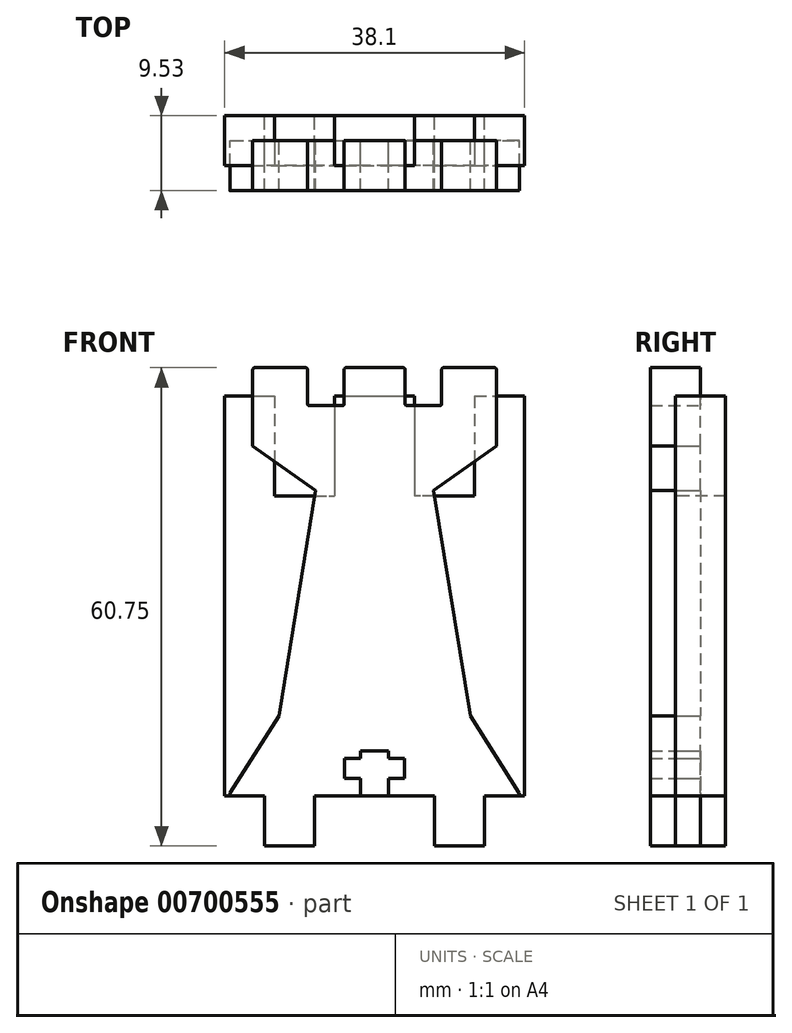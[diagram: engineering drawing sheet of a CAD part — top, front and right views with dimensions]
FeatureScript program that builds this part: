
annotation { "Feature Type Name" : "Feature", "Feature Type Description" : "" }
export const myFeature = defineFeature(function(context is Context, id is Id, definition is map)
    precondition{}
    {
        {
            var Q0;
            Q0=qCreatedBy(makeId("Front.planeOp"),FACE);
            var sketch = newSketch(context, id + "F0", { "sketchPlane" : qUnion([Q0])});
            skLineSegment(sketch, "E0.bottom", {"start": v(-6.35, 0) * mm, "end": v(7.62, 0) * mm});
            skLineSegment(sketch, "E1.bottom", {"start": v(-19.05, 0) * mm, "end": v(-13.97, 0) * mm});
            skLineSegment(sketch, "E1.top", {"start": v(-19.05, 50.8) * mm, "end": v(19.05, 50.8) * mm});
            skLineSegment(sketch, "E1.left", {"start": v(-19.05, 0) * mm, "end": v(-19.05, 50.8) * mm});
            skLineSegment(sketch, "E1.right", {"start": v(19.05, 0) * mm, "end": v(19.05, 50.8) * mm});
            skLineSegment(sketch, "E2.top", {"start": v(7.62, -6.35) * mm, "end": v(13.97, -6.35) * mm});
            skLineSegment(sketch, "E2.left", {"start": v(7.62, 0) * mm, "end": v(7.62, -6.35) * mm});
            skLineSegment(sketch, "E2.right", {"start": v(13.97, 0) * mm, "end": v(13.97, -6.35) * mm});
            skLineSegment(sketch, "E3.MirrorCS", {"start": v(6.35, 0) * mm, "end": v(-7.62, 0) * mm});
            skLineSegment(sketch, "E4.MirrorCS", {"start": v(19.05, 0) * mm, "end": v(13.97, 0) * mm});
            skLineSegment(sketch, "E5.MirrorCS", {"start": v(-7.62, -6.35) * mm, "end": v(-13.97, -6.35) * mm});
            skLineSegment(sketch, "E6.MirrorCS", {"start": v(-7.62, 0) * mm, "end": v(-7.62, -6.35) * mm});
            skLineSegment(sketch, "E7.MirrorCS", {"start": v(-13.97, 0) * mm, "end": v(-13.97, -6.35) * mm});
            skLineSegment(sketch, "E8.trimOffspring", {"start": v(-13.97, 0) * mm, "end": v(-19.05, 0) * mm});
            skLineSegment(sketch, "E9.trimOffspring", {"start": v(7.62, 0) * mm, "end": v(-6.35, 0) * mm});
            skLineSegment(sketch, "E10.trimOffspring", {"start": v(13.97, 0) * mm, "end": v(19.05, 0) * mm});
            skLineSegment(sketch, "E11.trimOffspring", {"start": v(-7.62, 0) * mm, "end": v(6.35, 0) * mm});
            skSolve(sketch);
        }
        {
            var Q0;
            Q0 = qSketchRegion(id + "F0", true);
            extrude(context, id + "F1", {"entities" : qUnion([Q0]), "depth" : 3.17 * mm, "offsetDistance" : 25.4 * mm, "hasSecondDirection" : true, "secondDirectionOppositeDirection" : true, "secondDirectionDepth" : 3.17 * mm});
        }
        {
            var Q0;
            Q0=makeQuery(id+"F1.opExtrude","CAP_FACE",FACE,{"disambiguationData":[OSD([sQuery(id+"F0.wireOp",EDGE,"E0.top"),sQuery(id+"F0.wireOp",EDGE,"E0.left"),sQuery(id+"F0.wireOp",EDGE,"E0.right"),sQuery(id+"F0.wireOp",EDGE,"E1.bottom"),sQuery(id+"F0.wireOp",EDGE,"E1.top"),sQuery(id+"F0.wireOp",EDGE,"E1.left"),sQuery(id+"F0.wireOp",EDGE,"E1.right")])],"isStart":false});
            var sketch = newSketch(context, id + "F2", { "sketchPlane" : qUnion([Q0])});
            skPoint(sketch, "E12.endSnap0", {"position": v(5.08, 50.8) * mm});
            skLineSegment(sketch, "E13", {"start": v(5.08, 50.8) * mm, "end": v(5.08, 38.1) * mm, "construction": true});
            skLineSegment(sketch, "E14", {"start": v(-5.08, 50.8) * mm, "end": v(-5.08, 38.1) * mm, "construction": true});
            skLineSegment(sketch, "E15", {"start": v(-12.7, 50.8) * mm, "end": v(-12.7, 38.1) * mm});
            skLineSegment(sketch, "E16", {"start": v(-12.7, 38.1) * mm, "end": v(-5.08, 38.1) * mm});
            skLineSegment(sketch, "E17", {"start": v(-5.08, 50.8) * mm, "end": v(-5.08, 38.1) * mm});
            skLineSegment(sketch, "E18", {"start": v(5.08, 50.8) * mm, "end": v(5.08, 38.1) * mm});
            skLineSegment(sketch, "E19", {"start": v(12.7, 50.8) * mm, "end": v(12.7, 38.1) * mm});
            skLineSegment(sketch, "E20", {"start": v(12.7, 38.1) * mm, "end": v(5.08, 38.1) * mm});
            skLineSegment(sketch, "E21", {"start": v(-12.7, 50.8) * mm, "end": v(-5.08, 50.8) * mm});
            skLineSegment(sketch, "E22", {"start": v(12.7, 50.8) * mm, "end": v(5.08, 50.8) * mm});
            skSolve(sketch);
        }
        {
            var Q0;
            Q0 = qSketchRegion(id + "F2", true);
            extrude(context, id + "F3", {"entities" : qUnion([Q0]), "operationType" : NewBodyOperationType.REMOVE, "oppositeDirection" : true, "depth" : 25.4 * mm, "offsetDistance" : 25.4 * mm});
        }
        {
            var Q0;
            Q0=qCreatedBy(makeId("Front.planeOp"),FACE);
            var sketch = newSketch(context, id + "F4", { "sketchPlane" : qUnion([Q0])});
            skLineSegment(sketch, "E23", {"start": v(-18.12, 0) * mm, "end": v(-13.97, 0) * mm});
            skLineSegment(sketch, "E24", {"start": v(-13.97, 0) * mm, "end": v(-13.97, -6.35) * mm});
            skLineSegment(sketch, "E25", {"start": v(-13.97, -6.35) * mm, "end": v(-7.62, -6.35) * mm});
            skLineSegment(sketch, "E26", {"start": v(-7.62, -6.35) * mm, "end": v(-7.62, 0) * mm});
            skLineSegment(sketch, "E27", {"start": v(-7.62, 0) * mm, "end": v(7.62, 0) * mm});
            skLineSegment(sketch, "E28", {"start": v(7.62, 0) * mm, "end": v(7.62, -6.35) * mm});
            skLineSegment(sketch, "E29", {"start": v(7.62, -6.35) * mm, "end": v(13.97, -6.35) * mm});
            skLineSegment(sketch, "E30", {"start": v(13.97, -6.35) * mm, "end": v(13.97, 0) * mm});
            skLineSegment(sketch, "E31", {"start": v(13.97, 0) * mm, "end": v(18.12, 0) * mm});
            skLineSegment(sketch, "E32", {"start": v(18.33, 0.39) * mm, "end": v(12.15, 10.17) * mm});
            skLineSegment(sketch, "E33", {"start": v(7.5, 38.81) * mm, "end": v(15.48, 44.47) * mm});
            skLineSegment(sketch, "E34", {"start": v(15.48, 44.47) * mm, "end": v(15.48, 54.15) * mm});
            skLineSegment(sketch, "E35", {"start": v(15.22, 54.4) * mm, "end": v(8.78, 54.4) * mm});
            skLineSegment(sketch, "E36", {"start": v(8.52, 54.15) * mm, "end": v(8.52, 49.82) * mm});
            skLineSegment(sketch, "E37", {"start": v(8.27, 49.57) * mm, "end": v(4.12, 49.57) * mm});
            skLineSegment(sketch, "E38", {"start": v(3.86, 49.82) * mm, "end": v(3.86, 54.15) * mm});
            skLineSegment(sketch, "E39", {"start": v(3.61, 54.4) * mm, "end": v(0, 54.4) * mm});
            skLineSegment(sketch, "E40.MirrorCS", {"start": v(13.97, 0) * mm, "end": v(13.97, -6.35) * mm});
            skLineSegment(sketch, "E41.MirrorCS", {"start": v(-3.86, 49.82) * mm, "end": v(-3.86, 54.15) * mm});
            skLineSegment(sketch, "E42.MirrorCS", {"start": v(-3.61, 54.4) * mm, "end": v(0, 54.4) * mm});
            skLineSegment(sketch, "E43.MirrorCS", {"start": v(13.97, -6.35) * mm, "end": v(7.62, -6.35) * mm});
            skLineSegment(sketch, "E44.MirrorCS", {"start": v(7.62, -6.35) * mm, "end": v(7.62, 0) * mm});
            skLineSegment(sketch, "E45.MirrorCS", {"start": v(-8.52, 54.15) * mm, "end": v(-8.52, 49.82) * mm});
            skLineSegment(sketch, "E46.MirrorCS", {"start": v(-8.27, 49.57) * mm, "end": v(-4.12, 49.57) * mm});
            skLineSegment(sketch, "E47.MirrorCS", {"start": v(-13.97, -6.35) * mm, "end": v(-13.97, 0) * mm});
            skLineSegment(sketch, "E48.MirrorCS", {"start": v(-7.62, -6.35) * mm, "end": v(-13.97, -6.35) * mm});
            skLineSegment(sketch, "E49.MirrorCS", {"start": v(-15.22, 54.4) * mm, "end": v(-8.78, 54.4) * mm});
            skLineSegment(sketch, "E50.MirrorCS", {"start": v(-7.62, 0) * mm, "end": v(-7.62, -6.35) * mm});
            skLineSegment(sketch, "E51.MirrorCS", {"start": v(-13.97, 0) * mm, "end": v(-18.12, 0) * mm});
            skLineSegment(sketch, "E52.MirrorCS", {"start": v(-18.33, 0.39) * mm, "end": v(-12.15, 10.17) * mm});
            skLineSegment(sketch, "E53.MirrorCS", {"start": v(-7.5, 38.81) * mm, "end": v(-15.48, 44.47) * mm});
            skLineSegment(sketch, "E54.MirrorCS", {"start": v(-15.48, 44.47) * mm, "end": v(-15.48, 54.15) * mm});
            skLineSegment(sketch, "E55.MirrorCS", {"start": v(7.62, 0) * mm, "end": v(-7.62, 0) * mm});
            skPoint(sketch, "E56.visualSharp", {"position": v(-15.48, 54.4) * mm});
            skArc(sketch, "E56.filletArc", {"start": v(-15.22, 54.4) * mm, "mid": v(-15.4, 54.33) * mm, "end": v(-15.48, 54.15) * mm});
            skPoint(sketch, "E57.visualSharp", {"position": v(-8.52, 54.4) * mm});
            skArc(sketch, "E57.filletArc", {"start": v(-8.52, 54.15) * mm, "mid": v(-8.6, 54.33) * mm, "end": v(-8.78, 54.4) * mm});
            skPoint(sketch, "E58.visualSharp", {"position": v(-8.52, 49.57) * mm});
            skArc(sketch, "E58.filletArc", {"start": v(-8.52, 49.82) * mm, "mid": v(-8.45, 49.64) * mm, "end": v(-8.27, 49.57) * mm});
            skPoint(sketch, "E59.visualSharp", {"position": v(-3.86, 54.4) * mm});
            skArc(sketch, "E59.filletArc", {"start": v(-3.61, 54.4) * mm, "mid": v(-3.79, 54.33) * mm, "end": v(-3.86, 54.15) * mm});
            skPoint(sketch, "E60.visualSharp", {"position": v(-3.86, 49.57) * mm});
            skArc(sketch, "E60.filletArc", {"start": v(-4.12, 49.57) * mm, "mid": v(-3.94, 49.64) * mm, "end": v(-3.86, 49.82) * mm});
            skPoint(sketch, "E61.visualSharp", {"position": v(3.86, 49.57) * mm});
            skArc(sketch, "E61.filletArc", {"start": v(3.86, 49.82) * mm, "mid": v(3.94, 49.64) * mm, "end": v(4.12, 49.57) * mm});
            skPoint(sketch, "E62.visualSharp", {"position": v(8.52, 49.57) * mm});
            skArc(sketch, "E62.filletArc", {"start": v(8.27, 49.57) * mm, "mid": v(8.45, 49.64) * mm, "end": v(8.52, 49.82) * mm});
            skPoint(sketch, "E63.visualSharp", {"position": v(3.86, 54.4) * mm});
            skArc(sketch, "E63.filletArc", {"start": v(3.86, 54.15) * mm, "mid": v(3.79, 54.33) * mm, "end": v(3.61, 54.4) * mm});
            skPoint(sketch, "E64.visualSharp", {"position": v(8.52, 54.4) * mm});
            skArc(sketch, "E64.filletArc", {"start": v(8.78, 54.4) * mm, "mid": v(8.6, 54.33) * mm, "end": v(8.52, 54.15) * mm});
            skPoint(sketch, "E65.visualSharp", {"position": v(15.48, 54.4) * mm});
            skArc(sketch, "E65.filletArc", {"start": v(15.48, 54.15) * mm, "mid": v(15.4, 54.33) * mm, "end": v(15.22, 54.4) * mm});
            skLineSegment(sketch, "E66", {"start": v(-7.5, 38.81) * mm, "end": v(-12.15, 10.17) * mm});
            skLineSegment(sketch, "E67", {"start": v(7.5, 38.81) * mm, "end": v(12.15, 10.17) * mm});
            skArc(sketch, "E68.filletArc", {"start": v(-18.33, 0.39) * mm, "mid": v(-18.34, 0.13) * mm, "end": v(-18.12, 0) * mm});
            skArc(sketch, "E69.filletArc", {"start": v(18.12, 0) * mm, "mid": v(18.34, 0.13) * mm, "end": v(18.33, 0.39) * mm});
            skLineSegment(sketch, "E70.trimOffspring", {"start": v(18.12, 0) * mm, "end": v(13.97, 0) * mm});
            skLineSegment(sketch, "E71", {"start": v(-15.48, 44.47) * mm, "end": v(-15.48, 0) * mm, "construction": true});
            skLineSegment(sketch, "E72", {"start": v(-7.5, 38.81) * mm, "end": v(-7.62, 0) * mm, "construction": true});
            skLineSegment(sketch, "E73", {"start": v(-8.27, 49.82) * mm, "end": v(-8.27, -6.35) * mm, "construction": true});
            skLineSegment(sketch, "E74", {"start": v(-15.22, 54.15) * mm, "end": v(-15.48, 0) * mm, "construction": true});
            skLineSegment(sketch, "E75", {"start": v(-3.86, 49.82) * mm, "end": v(-3.86, 0) * mm, "construction": true});
            skSolve(sketch);
        }
        {
            var Q0;
            Q0 = qSketchRegion(id + "F4", true);
            extrude(context, id + "F5", {"entities" : qUnion([Q0]), "depth" : 6.35 * mm, "offsetDistance" : 25.4 * mm});
        }
        {
            var Q0;
            Q0=qCreatedBy(makeId("Front.planeOp"),FACE);
            var sketch = newSketch(context, id + "F6", { "sketchPlane" : qUnion([Q0])});
            skLineSegment(sketch, "E76.bottom", {"start": v(-1.78, 5.72) * mm, "end": v(1.78, 5.72) * mm});
            skLineSegment(sketch, "E76.left", {"start": v(-1.78, 5.72) * mm, "end": v(-1.78, 4.76) * mm});
            skLineSegment(sketch, "E77", {"start": v(0, 5.72) * mm, "end": v(0, 9.6) * mm, "construction": true});
            skLineSegment(sketch, "E78.bottom", {"start": v(-1.78, 4.76) * mm, "end": v(-3.8, 4.76) * mm});
            skLineSegment(sketch, "E78.top", {"start": v(-1.78, 2.22) * mm, "end": v(-3.8, 2.22) * mm});
            skLineSegment(sketch, "E78.right", {"start": v(-3.8, 4.76) * mm, "end": v(-3.8, 2.22) * mm});
            skLineSegment(sketch, "E79.top", {"start": v(-1.78, 0) * mm, "end": v(1.78, 0) * mm});
            skLineSegment(sketch, "E79.left", {"start": v(-1.78, 2.22) * mm, "end": v(-1.78, 0) * mm});
            skLineSegment(sketch, "E80.MirrorCS", {"start": v(3.81, 4.76) * mm, "end": v(3.81, 2.22) * mm});
            skLineSegment(sketch, "E81.MirrorCS", {"start": v(1.78, 5.72) * mm, "end": v(1.78, 4.76) * mm});
            skLineSegment(sketch, "E82.MirrorCS", {"start": v(1.78, 2.22) * mm, "end": v(1.78, 0) * mm});
            skLineSegment(sketch, "E83.MirrorCS", {"start": v(1.78, 4.76) * mm, "end": v(3.81, 4.76) * mm});
            skLineSegment(sketch, "E84.MirrorCS", {"start": v(1.78, 0) * mm, "end": v(-1.78, 0) * mm});
            skLineSegment(sketch, "E85.MirrorCS", {"start": v(1.78, 2.22) * mm, "end": v(3.81, 2.22) * mm});
            skLineSegment(sketch, "E86.MirrorCS", {"start": v(1.78, 5.72) * mm, "end": v(-1.78, 5.72) * mm});
            skSolve(sketch);
        }
        {
            var Q0;
            Q0 = qSketchRegion(id + "F6", true);
            extrude(context, id + "F7", {"entities" : qUnion([Q0]), "operationType" : NewBodyOperationType.REMOVE, "depth" : 25.4 * mm, "offsetDistance" : 25.4 * mm});
        }
    });
